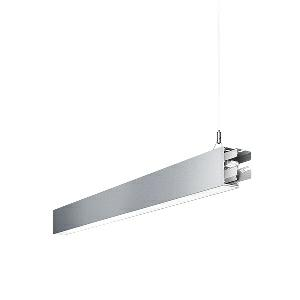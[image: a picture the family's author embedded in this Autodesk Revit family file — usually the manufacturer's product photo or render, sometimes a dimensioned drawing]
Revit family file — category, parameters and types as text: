
# Revit family: idoo_line_-_ilp_4000_840_d_mid_00805700_030e
name_source: partatom
category: Lighting Fixtures
units: mm (PartAtom-declared; Revit-internal decimal feet)

## family parameters
Cut with Voids When Loaded = No
Host = Face
Light Source = No
Part Type = Normal
Room Calculation Point = No
Round Connector Dimension = Use Diameter
Shared = No

## types (1)
- IDOO.line - ILP 4000/840/D MID (1 x LED, 3950 lm, 4000K)
    Apparent Load = 29 VA
    Approval mark = CE
    CIE Flux Codes = 66 91 98 40 100
    Color Rendering = 80-89
    Color Temperature = 4000K
    Control Gear = Electronic ballast
    Default Elevation = 1800 mm
    Description = ILP 4000/840/D|Suspended luminaire|light source: LED|connected load: 220-240 V, 50/60 Hz|Power consumption: approx. 29 W|standby: approx. 0,15|luminous flux: 3950 lm|luminous efficacy: 136 lm/W|light distribution: Direct/indirect|direct ratio: approx. 40 %|colour temperature: Cold white, ca. 4000 K|color rendering index (CRI): >= 80|chromaticity tolerance:  3 SDCM|System of protection: IP 40|technology: Continuously dimmable|luminaire body|material: Sectional aluminium|colour: Silver|lamp cover: Acrylic (PMMA), Clear|mains lead: 1,0 m With free stranded wires|Fastening: Steel cable 0.3 - 0.7 m|glare control: Prism aperture|luminance(L65): <= 2700 cd/m|unified glare rating(4H 8H): <=  16|special features: DALI Load 1x, TouchDIM - dimming via standard switch, Through-wired, up to 18 m on one mains connection, Flicker-free, Suitable as emergency lighting, Mechanical and electrical connection of the individual modules without tools|
    Frequency = 50 Hz
    Height = 110 mm
    Lamp = 1 x LED
    Lamp Light Flux = 3950 lm
    Lamp count = 1
    Length = 1402 mm
    Luminous efficacy = 136 lm/W
    Manufacturer = Waldmann
    ModVariant = No
    Model = 00805700
    Mounting Place = Ceiling
    Mounting Type = Pendant
    Number of Poles = 1
    OnlyDefault = Yes
    Power Factor = 1
    Product Name = IDOO.line - ILP 4000/840/D MID
    Product group = Suspended luminaire
    ProductGroupID = 9
    Protection Class = Protection class I
    Protection Degree = IP 40
    RLX_Detail_Level = 1
    RLX_Emergency_Light_Flux = 0 lm
    RLX_Emergency_Type = 0
    RLX_Emergency_Type_DB = No
    RlxData = <blob elided: 21777 chars, md5=582fd2f1>
    Socket = socket
    Standby Power = 0 W
    System Light Flux = 3950 lm
    System Power = 29 W
    Type Comments = Product without accessories
    Type Image = 113311000-00692597.jpg
    URL = http://relux.com
    VarID = ---
    Voltage = 230 V
    Voltage Range = 220-240 V
    Weight = 0.00 kg
    Width = 60 mm  [stored 0.19685 ft]

note: [stored X ft] marks values corroborated as IEEE doubles in the binary element streams (Revit-internal decimal feet)

## geometry (parser evidence)
native form markers: Blend x4, Sweep x13
no freeform markers — native parametric forms only
